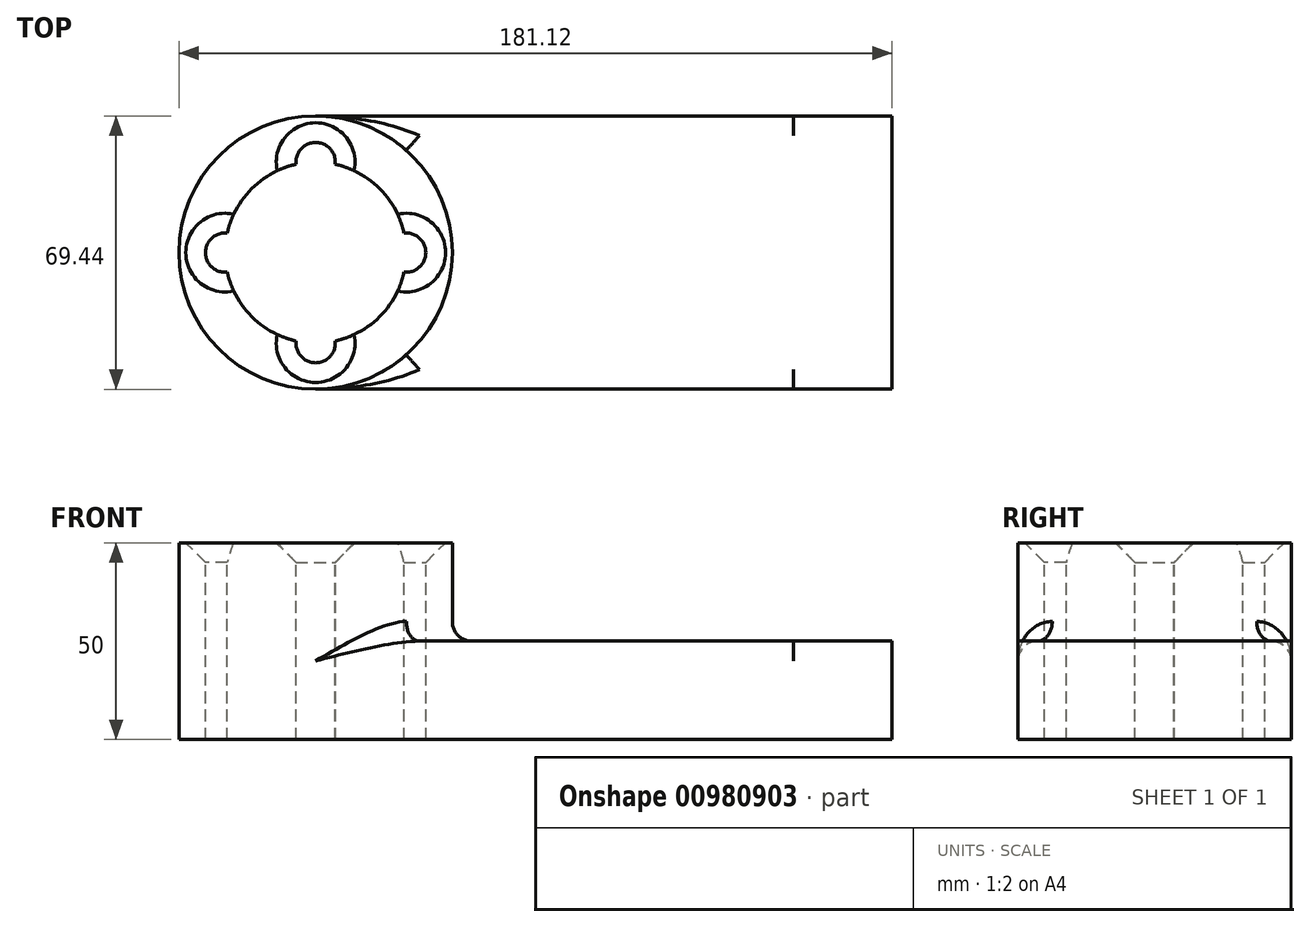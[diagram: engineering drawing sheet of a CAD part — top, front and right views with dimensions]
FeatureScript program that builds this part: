
annotation { "Feature Type Name" : "Feature", "Feature Type Description" : "" }
export const myFeature = defineFeature(function(context is Context, id is Id, definition is map)
    precondition{}
    {
        {
            var Q0;
            Q0=qCreatedBy(makeId("Top.planeOp"),FACE);
            var sketch = newSketch(context, id + "F0", { "sketchPlane" : qUnion([Q0])});
            skLineSegment(sketch, "E0.bottom", {"start": v(60.7, -34.72) * mm, "end": v(-60.7, -34.72) * mm});
            skLineSegment(sketch, "E0.top", {"start": v(60.7, 34.72) * mm, "end": v(-60.7, 34.72) * mm});
            skLineSegment(sketch, "E0.left", {"start": v(60.7, -34.72) * mm, "end": v(60.7, 34.72) * mm});
            skLineSegment(sketch, "E0.right", {"start": v(-60.7, -34.72) * mm, "end": v(-60.7, 34.72) * mm});
            skPoint(sketch, "E0.middle", {"position": v(0, 0) * mm});
            skPoint(sketch, "E1", {"position": v(-60.7, 0) * mm});
            skCircle(sketch, "E2", {"center": v(-60.7, 0) * mm, "radius": 34.72 * mm});
            skCircle(sketch, "E3", {"center": v(-60.7, 0) * mm, "radius": 23 * mm});
            skSolve(sketch);
        }
        {
            var Q0;
            {var subQ0=sQuery(id+"F0.wireOp",EDGE,"E0.bottom");Q0=makeQuery(id+"F0.imprint","IMPRINT",FACE,{"disambiguationData":[TD([[makeQuery(id+"F0.imprint","IMPRINT",EDGE,{"derivedFrom":subQ0}),-1.0]])]});}
            var Q1;
            {var subQ1=sQuery(id+"F0.wireOp",EDGE,"E0.right");var subQ3=sQuery(id+"F0.wireOp",EDGE,"E3");var subQ4=makeQuery(id+"F0.imprint","INTERSECT",VERTEX,{"disambiguationData":[OD(0.0)],"derivedFrom":[subQ1,subQ3]});Q1=makeQuery(id+"F0.imprint","IMPRINT",FACE,{"disambiguationData":[TD([[makeQuery(id+"F0.imprint","IMPRINT",EDGE,{"disambiguationData":[TD([[subQ4,1.0]])],"derivedFrom":subQ3}),-1.0]])]});}
            var Q2;
            {var subQ1=sQuery(id+"F0.wireOp",EDGE,"E0.right");var subQ3=sQuery(id+"F0.wireOp",EDGE,"E3");var subQ4=makeQuery(id+"F0.imprint","INTERSECT",VERTEX,{"disambiguationData":[OD(0.0)],"derivedFrom":[subQ1,subQ3]});Q2=makeQuery(id+"F0.imprint","IMPRINT",FACE,{"disambiguationData":[TD([[makeQuery(id+"F0.imprint","IMPRINT",EDGE,{"disambiguationData":[TD([[subQ4,-1.0]])],"derivedFrom":subQ3}),-1.0]])]});}
            extrude(context, id + "F1", {"entities" : qUnion([Q0, Q1, Q2]), "depth" : 25 * mm, "offsetDistance" : 25 * mm});
        }
        {
            var Q0;
            {var subQ1=sQuery(id+"F0.wireOp",EDGE,"E0.right");var subQ3=sQuery(id+"F0.wireOp",EDGE,"E3");var subQ4=makeQuery(id+"F0.imprint","INTERSECT",VERTEX,{"disambiguationData":[OD(0.0)],"derivedFrom":[subQ1,subQ3]});Q0=makeQuery(id+"F0.imprint","IMPRINT",FACE,{"disambiguationData":[TD([[makeQuery(id+"F0.imprint","IMPRINT",EDGE,{"disambiguationData":[TD([[subQ4,1.0]])],"derivedFrom":subQ3}),-1.0]])]});}
            var Q1;
            {var subQ1=sQuery(id+"F0.wireOp",EDGE,"E0.right");var subQ3=sQuery(id+"F0.wireOp",EDGE,"E3");var subQ4=makeQuery(id+"F0.imprint","INTERSECT",VERTEX,{"disambiguationData":[OD(0.0)],"derivedFrom":[subQ1,subQ3]});Q1=makeQuery(id+"F0.imprint","IMPRINT",FACE,{"disambiguationData":[TD([[makeQuery(id+"F0.imprint","IMPRINT",EDGE,{"disambiguationData":[TD([[subQ4,-1.0]])],"derivedFrom":subQ3}),-1.0]])]});}
            extrude(context, id + "F2", {"entities" : qUnion([Q0, Q1]), "operationType" : NewBodyOperationType.ADD, "depth" : 50 * mm, "offsetDistance" : 25 * mm});
        }
        {
            var Q0;
            {var subQ0=sQuery(id+"F0.wireOp",EDGE,"E2");Q0=makeQuery(id+"F2.boolean.opBoolean","INTERSECT",EDGE,{"derivedFrom":[makeQuery(id+"F1.opExtrude","CAP_FACE",FACE,{"disambiguationData":[OSD([sQuery(id+"F0.wireOp",EDGE,"E0.bottom"),sQuery(id+"F0.wireOp",EDGE,"E0.top"),sQuery(id+"F0.wireOp",EDGE,"E0.left"),subQ0,sQuery(id+"F0.wireOp",EDGE,"E3")])],"isStart":false}),makeQuery(id+"F2.opExtrude","SWEPT_FACE",FACE,{"disambiguationData":[OSD([subQ0])]})]});}
            var Q1;
            Q1=makeQuery(id+"F1.opExtrude","CAP_EDGE",EDGE,{"disambiguationData":[OSD([sQuery(id+"F0.wireOp",EDGE,"E0.bottom")])],"isStart":false});
            var Q2;
            Q2=makeQuery(id+"F1.opExtrude","CAP_EDGE",EDGE,{"disambiguationData":[OSD([sQuery(id+"F0.wireOp",EDGE,"E0.top")])],"isStart":false});
            fillet(context, id + "F3", {"entities" : qUnion([Q0, Q1, Q2]), "radius" : 5 * mm, "tangentPropagation" : true, "allowEdgeOverflow" : false});
        }
        {
            var Q0;
            Q0=makeQuery(id+"F1.opExtrude","SWEPT_FACE",FACE,{"disambiguationData":[OSD([sQuery(id+"F0.wireOp",EDGE,"E0.left")])]});
            var sketch = newSketch(context, id + "F4", { "sketchPlane" : qUnion([Q0])});
            skLineSegment(sketch, "E4.bottom", {"start": v(-34.72, 0) * mm, "end": v(34.72, 0) * mm});
            skLineSegment(sketch, "E4.top", {"start": v(-34.72, 25) * mm, "end": v(34.72, 25) * mm});
            skLineSegment(sketch, "E4.left", {"start": v(-34.72, 0) * mm, "end": v(-34.72, 25) * mm});
            skLineSegment(sketch, "E4.right", {"start": v(34.72, 0) * mm, "end": v(34.72, 25) * mm});
            skSolve(sketch);
        }
        {
            var Q0;
            {var subQ1=makeQuery(id+"F3.opFillet","BLEND_EDGE",EDGE,{"blendedFrom":[makeQuery(id+"F1.opExtrude","CAP_EDGE",EDGE,{"disambiguationData":[OSD([sQuery(id+"F0.wireOp",EDGE,"E0.bottom")])],"isStart":false}),makeQuery(id+"F1.opExtrude","SWEPT_FACE",FACE,{"disambiguationData":[OSD([sQuery(id+"F0.wireOp",EDGE,"E0.left")])]})],"blendedInto":[makeQuery(id+"F1.opExtrude","SWEPT_FACE",FACE,{"disambiguationData":[OSD([sQuery(id+"F0.wireOp",EDGE,"E0.left")])]})]});Q0=makeQuery(id+"F4.imprint","IMPRINT",FACE,{"disambiguationData":[TD([[makeQuery(id+"F4.imprint","IMPRINT",EDGE,{"derivedFrom":subQ1}),-1.0]])]});}
            var Q1;
            {var subQ1=sQuery(id+"F4.wireOp",EDGE,"E4.bottom");Q1=makeQuery(id+"F4.imprint","IMPRINT",FACE,{"disambiguationData":[TD([[makeQuery(id+"F4.imprint","IMPRINT",EDGE,{"derivedFrom":subQ1}),1.0]])]});}
            var Q2;
            {var subQ1=makeQuery(id+"F3.opFillet","BLEND_EDGE",EDGE,{"blendedFrom":[makeQuery(id+"F1.opExtrude","CAP_EDGE",EDGE,{"disambiguationData":[OSD([sQuery(id+"F0.wireOp",EDGE,"E0.top")])],"isStart":false}),makeQuery(id+"F1.opExtrude","SWEPT_FACE",FACE,{"disambiguationData":[OSD([sQuery(id+"F0.wireOp",EDGE,"E0.left")])]})],"blendedInto":[makeQuery(id+"F1.opExtrude","SWEPT_FACE",FACE,{"disambiguationData":[OSD([sQuery(id+"F0.wireOp",EDGE,"E0.left")])]})]});Q2=makeQuery(id+"F4.imprint","IMPRINT",FACE,{"disambiguationData":[TD([[makeQuery(id+"F4.imprint","IMPRINT",EDGE,{"derivedFrom":subQ1}),-1.0]])]});}
            extrude(context, id + "F5", {"entities" : qUnion([Q0, Q1, Q2]), "operationType" : NewBodyOperationType.ADD, "depth" : 25 * mm, "offsetDistance" : 25 * mm});
        }
        {
            var Q0;
            Q0=makeQuery(id+"F2.opExtrude","CAP_FACE",FACE,{"disambiguationData":[OSD([sQuery(id+"F0.wireOp",EDGE,"E2"),sQuery(id+"F0.wireOp",EDGE,"E3")])],"isStart":false});
            var sketch = newSketch(context, id + "F6", { "sketchPlane" : qUnion([Q0])});
            skPoint(sketch, "E5", {"position": v(-37.71, 0) * mm});
            skPoint(sketch, "E6", {"position": v(-83.7, 0) * mm});
            skLineSegment(sketch, "E7", {"start": v(-83.7, 0) * mm, "end": v(-37.71, 0) * mm});
            skLineSegment(sketch, "E8", {"start": v(-60.7, 0) * mm, "end": v(-60.7, 23) * mm});
            skLineSegment(sketch, "E9", {"start": v(-60.7, 23) * mm, "end": v(-60.7, -23) * mm});
            skPoint(sketch, "E10", {"position": v(-60.7, 23) * mm});
            skPoint(sketch, "E11", {"position": v(-60.7, -23) * mm});
            skSolve(sketch);
        }
        {
            var Q0;
            Q0=sQuery(id+"F6.wireOp",VERTEX,"E6");
            var Q1;
            Q1=sQuery(id+"F6.wireOp",VERTEX,"E10");
            var Q2;
            Q2=sQuery(id+"F6.wireOp",VERTEX,"E5");
            var Q3;
            Q3=sQuery(id+"F6.wireOp",VERTEX,"E11");
            var Q4;
            Q4=makeQuery(id+"F1.opExtrude","SWEPT_BODY",BODY,{"disambiguationData":[OSD([sQuery(id+"F0.wireOp",EDGE,"E0.bottom"),sQuery(id+"F0.wireOp",EDGE,"E0.top"),sQuery(id+"F0.wireOp",EDGE,"E0.left"),sQuery(id+"F0.wireOp",EDGE,"E2"),sQuery(id+"F0.wireOp",EDGE,"E3")])]});
            hole(context, id + "F7", {"style" : HoleStyle.C_SINK, "endStyle" : HoleEndStyle.THROUGH, "holeDiameter" : 10 * mm, "cSinkDiameter" : 20 * mm, "cSinkAngle" : 90 * degree, "majorDiameter" : 5 * mm, "isTappedThrough" : true, "tappedDepth" : 12 * mm, "tapClearance" : 3, "locations" : qUnion([Q0, Q1, Q2, Q3]), "scope" : qUnion([Q4])});
        }
    });
